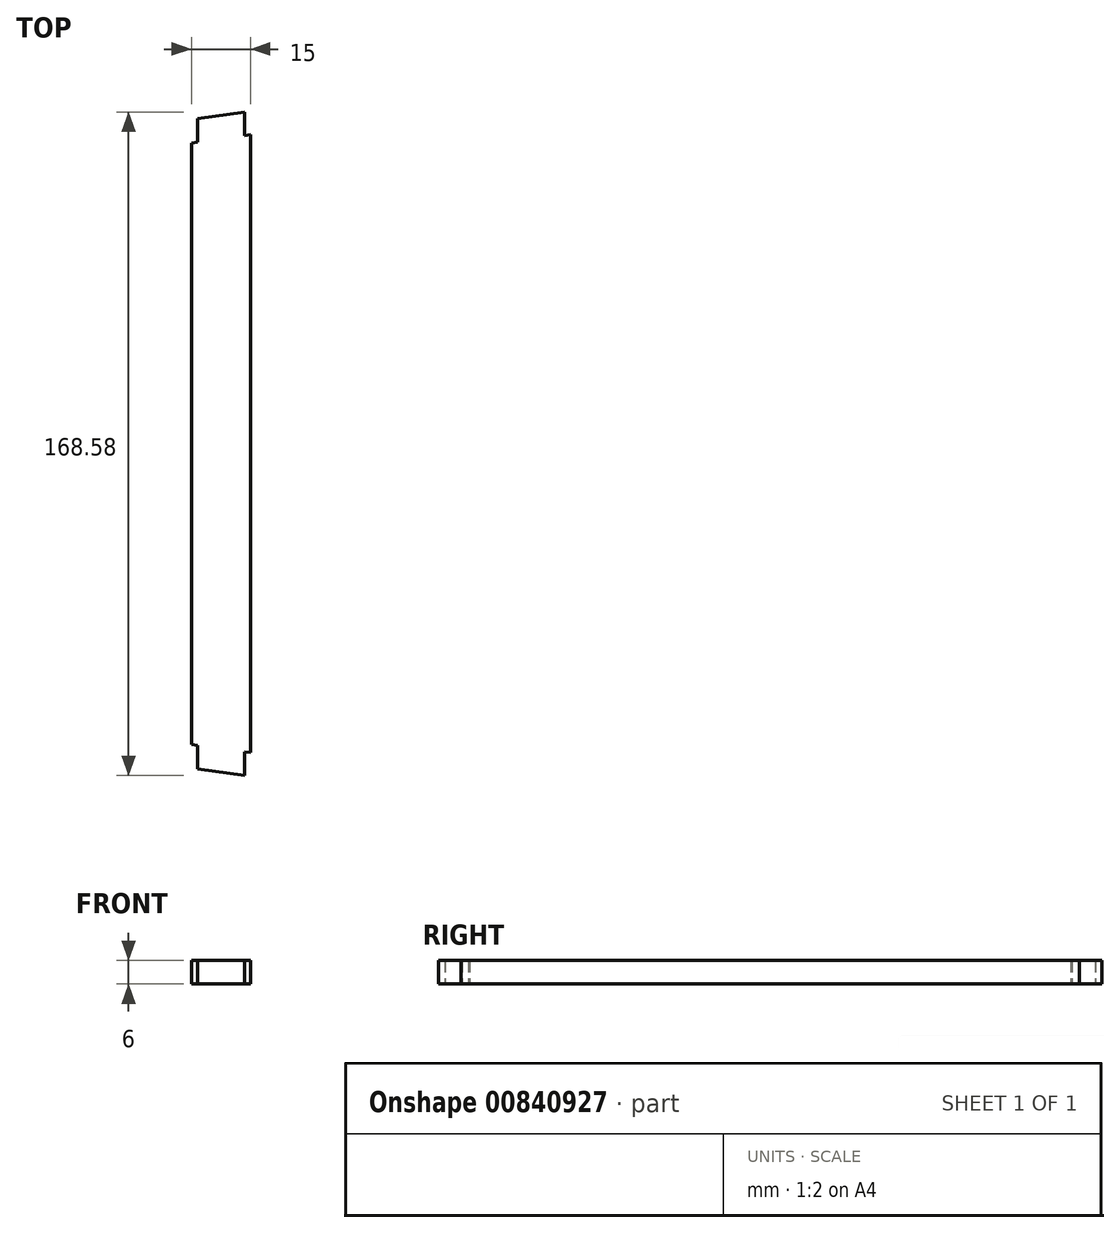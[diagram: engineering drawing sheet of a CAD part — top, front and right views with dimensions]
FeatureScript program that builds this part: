
annotation { "Feature Type Name" : "Feature", "Feature Type Description" : "" }
export const myFeature = defineFeature(function(context is Context, id is Id, definition is map)
    precondition{}
    {
        {
            var Q0;
            Q0=qCreatedBy(makeId("Top.planeOp"),FACE);
            var sketch = newSketch(context, id + "F0", { "sketchPlane" : qUnion([Q0])});
            skLineSegment(sketch, "E0", {"start": v(0, 0) * mm, "end": v(0, 77.45) * mm, "construction": true});
            skLineSegment(sketch, "E1", {"start": v(0, 0) * mm, "end": v(-49.4, 0) * mm, "construction": true});
            skLineSegment(sketch, "E2", {"start": v(0, 77.45) * mm, "end": v(-27, 73.66) * mm, "construction": true});
            skLineSegment(sketch, "E3", {"start": v(-7.5, 0) * mm, "end": v(-7.5, 76.4) * mm});
            skLineSegment(sketch, "E4", {"start": v(-7.5, 76.4) * mm, "end": v(-6, 76.6) * mm});
            skLineSegment(sketch, "E5", {"start": v(-6, 76.6) * mm, "end": v(-6, 82.6) * mm});
            skLineSegment(sketch, "E6", {"start": v(-6, 82.6) * mm, "end": v(6, 84.3) * mm});
            skLineSegment(sketch, "E7", {"start": v(6, 84.3) * mm, "end": v(6, 78.3) * mm});
            skLineSegment(sketch, "E8", {"start": v(6, 78.3) * mm, "end": v(7.5, 78.5) * mm});
            skLineSegment(sketch, "E9", {"start": v(7.5, 78.5) * mm, "end": v(7.5, 0) * mm});
            skLineSegment(sketch, "E10", {"start": v(0, 77.45) * mm, "end": v(0, 83.45) * mm, "construction": true});
            skLineSegment(sketch, "E11.MirrorCS", {"start": v(-7.5, -76.4) * mm, "end": v(-6, -76.6) * mm});
            skLineSegment(sketch, "E12.MirrorCS", {"start": v(-6, -76.6) * mm, "end": v(-6, -82.6) * mm});
            skLineSegment(sketch, "E13.MirrorCS", {"start": v(6, -84.3) * mm, "end": v(6, -78.3) * mm});
            skLineSegment(sketch, "E14.MirrorCS", {"start": v(6, -78.3) * mm, "end": v(7.5, -78.5) * mm});
            skLineSegment(sketch, "E15.MirrorCS", {"start": v(0, -77.45) * mm, "end": v(0, -83.45) * mm, "construction": true});
            skLineSegment(sketch, "E16.MirrorCS", {"start": v(-6, -82.6) * mm, "end": v(6, -84.3) * mm});
            skLineSegment(sketch, "E17.MirrorCS", {"start": v(0, -77.45) * mm, "end": v(-27, -73.66) * mm, "construction": true});
            skLineSegment(sketch, "E18.MirrorCS", {"start": v(0, 0) * mm, "end": v(0, -77.45) * mm, "construction": true});
            skLineSegment(sketch, "E19.MirrorCS", {"start": v(-7.5, 0) * mm, "end": v(-7.5, -76.4) * mm});
            skLineSegment(sketch, "E20.MirrorCS", {"start": v(7.5, -78.5) * mm, "end": v(7.5, 0) * mm});
            skSolve(sketch);
        }
        {
            var Q0;
            Q0=qSketchRegion(id+"F0",true);
            extrude(context, id + "F1", {"entities" : qUnion([Q0]), "depth" : 6 * mm, "offsetDistance" : 25 * mm});
        }
    });
